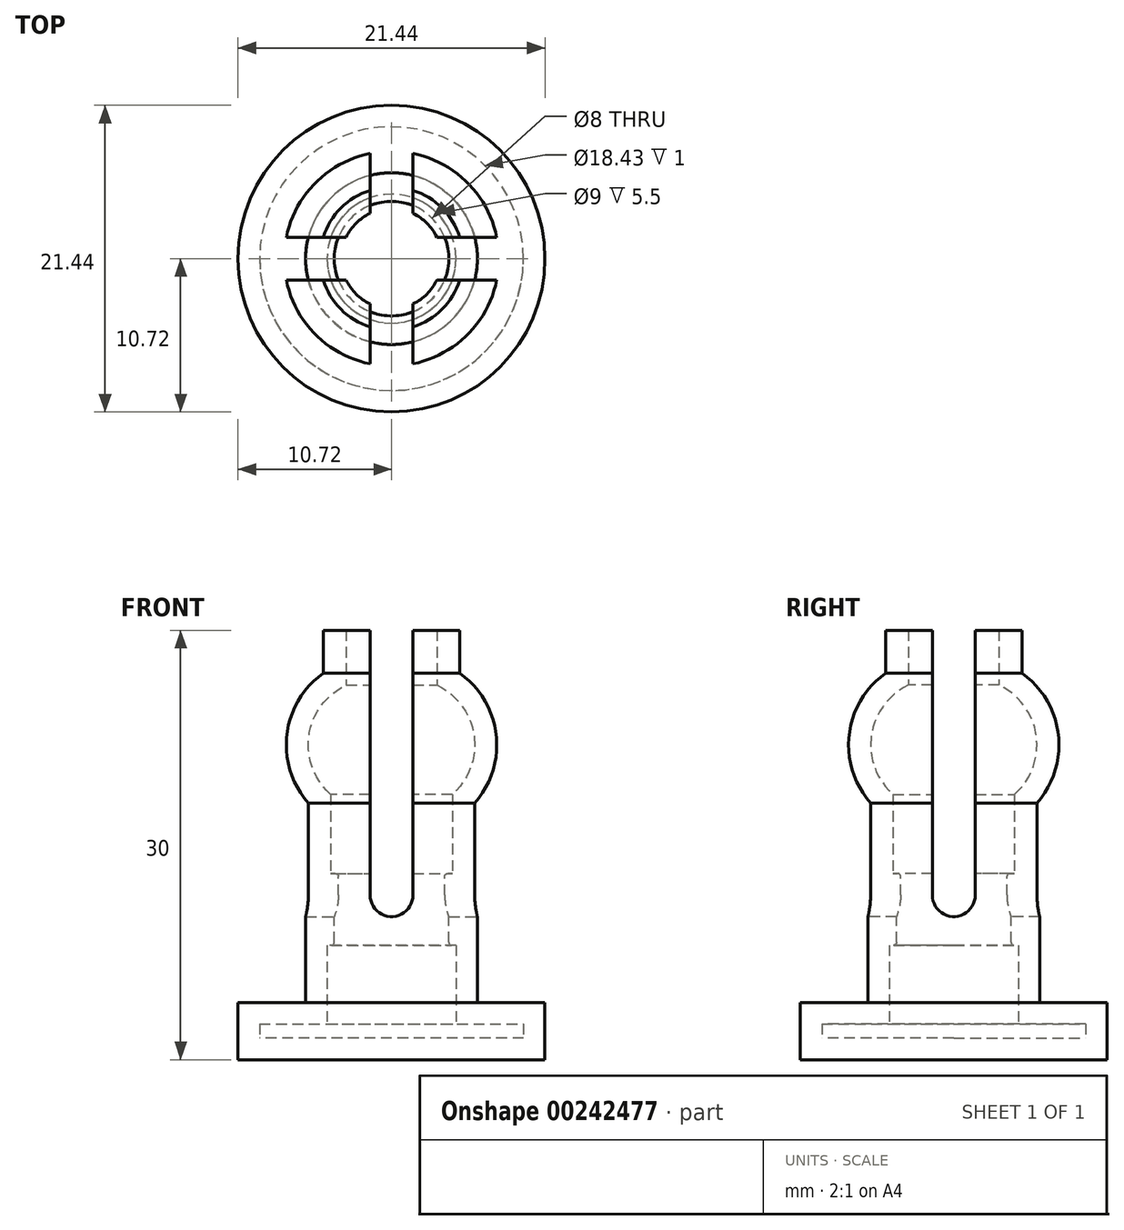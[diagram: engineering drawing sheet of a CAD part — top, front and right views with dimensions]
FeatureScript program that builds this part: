
annotation { "Feature Type Name" : "Feature", "Feature Type Description" : "" }
export const myFeature = defineFeature(function(context is Context, id is Id, definition is map)
    precondition{}
    {
        {
            var Q0;
            Q0=qCreatedBy(makeId("Front.planeOp"),FACE);
            var sketch = newSketch(context, id + "F0", { "sketchPlane" : qUnion([Q0])});
            skLineSegment(sketch, "E0", {"start": v(0, 8.33) * mm, "end": v(5, 8.33) * mm});
            skLineSegment(sketch, "E1", {"start": v(5, 8.33) * mm, "end": v(5, 5.33) * mm});
            skArc(sketch, "E2", {"start": v(6, -3.73) * mm, "mid": v(7.46, 1.02) * mm, "end": v(5, 5.33) * mm});
            skLineSegment(sketch, "E3", {"start": v(6, -17.67) * mm, "end": v(10.72, -17.67) * mm});
            skLineSegment(sketch, "E4", {"start": v(10.72, -17.67) * mm, "end": v(10.72, -21.67) * mm});
            skLineSegment(sketch, "E5", {"start": v(10.72, -21.67) * mm, "end": v(0, -21.67) * mm});
            skLineSegment(sketch, "E6", {"start": v(0, -21.67) * mm, "end": v(0, 8.33) * mm});
            skLineSegment(sketch, "E7", {"start": v(0, 22.23) * mm, "end": v(0, -23.28) * mm, "construction": true});
            skLineSegment(sketch, "E8", {"start": v(6, -17.67) * mm, "end": v(6, -3.73) * mm});
            skPoint(sketch, "E9.start.orphan", {"position": v(5, -4.67) * mm});
            skSolve(sketch);
        }
        {
            var Q0;
            Q0=qCreatedBy(makeId("Front.planeOp"),FACE);
            var sketch = newSketch(context, id + "F1", { "sketchPlane" : qUnion([Q0])});
            skLineSegment(sketch, "E10", {"start": v(0, 8.33) * mm, "end": v(5, 8.33) * mm});
            skLineSegment(sketch, "E11", {"start": v(5, 8.33) * mm, "end": v(5, 5.33) * mm});
            skArc(sketch, "E12", {"start": v(6, -3.73) * mm, "mid": v(7.46, 1.02) * mm, "end": v(5, 5.33) * mm});
            skLineSegment(sketch, "E13", {"start": v(6, -17.67) * mm, "end": v(10.72, -17.67) * mm});
            skLineSegment(sketch, "E14", {"start": v(10.72, -17.67) * mm, "end": v(10.72, -21.67) * mm});
            skLineSegment(sketch, "E15", {"start": v(10.72, -21.67) * mm, "end": v(0, -21.67) * mm});
            skLineSegment(sketch, "E16", {"start": v(0, -21.67) * mm, "end": v(0, 8.33) * mm});
            skLineSegment(sketch, "E17", {"start": v(0, 21.89) * mm, "end": v(0, -23.62) * mm, "construction": true});
            skLineSegment(sketch, "E18", {"start": v(6, -3.73) * mm, "end": v(6, -17.67) * mm});
            skSolve(sketch);
        }
        {
            var Q0;
            Q0=qCreatedBy(makeId("Front.planeOp"),FACE);
            var sketch = newSketch(context, id + "F2", { "sketchPlane" : qUnion([Q0])});
            skArc(sketch, "E19.0", {"start": v(7, -2.8) * mm, "mid": v(7.67, 1.65) * mm, "end": v(5.3, 5.48) * mm});
            skLineSegment(sketch, "E20.0", {"start": v(5.3, 8.63) * mm, "end": v(5.3, 5.48) * mm});
            skLineSegment(sketch, "E21.0", {"start": v(0, 8.63) * mm, "end": v(5.3, 8.63) * mm});
            skArc(sketch, "E22", {"start": v(0, 12.9) * mm, "mid": v(11.42, 4.57) * mm, "end": v(7, -8.85) * mm});
            skLineSegment(sketch, "E23", {"start": v(0, 12.9) * mm, "end": v(0, 8.63) * mm});
            skLineSegment(sketch, "E24", {"start": v(7, -8.85) * mm, "end": v(7, -2.8) * mm});
            skSolve(sketch);
        }
        {
            var Q0;
            Q0=makeQuery(id+"F0.imprint","IMPRINT",FACE,{"disambiguationData":[TD([[makeQuery(id+"F0.imprint","IMPRINT",EDGE,{"derivedFrom":sQuery(id+"F0.wireOp",EDGE,"E0")}),-1.0]])]});
            var Q1;
            Q1=sQuery(id+"F1.wireOp",EDGE,"E16");
            revolve(context, id + "F3", {"entities" : qUnion([Q0]), "axis" : qUnion([Q1]), "revolveType" : RevolveType.FULL});
        }
        {
            var Q0;
            Q0=makeQuery(id+"F2.imprint","IMPRINT",FACE,{"disambiguationData":[TD([[makeQuery(id+"F2.imprint","IMPRINT",EDGE,{"derivedFrom":sQuery(id+"F2.wireOp",EDGE,"E19.0")}),-1.0]])]});
            var Q1;
            Q1=sQuery(id+"F2.wireOp",EDGE,"E23");
            revolve(context, id + "F4", {"entities" : qUnion([Q0]), "axis" : qUnion([Q1]), "revolveType" : RevolveType.FULL});
        }
        {
            var Q0;
            Q0=qCreatedBy(makeId("Front.planeOp"),FACE);
            var sketch = newSketch(context, id + "F5", { "sketchPlane" : qUnion([Q0])});
            skLineSegment(sketch, "E25.bottom", {"start": v(-1.5, 8.33) * mm, "end": v(1.5, 8.33) * mm});
            skLineSegment(sketch, "E25.left", {"start": v(-1.5, 8.33) * mm, "end": v(-1.5, -10.17) * mm});
            skLineSegment(sketch, "E25.right", {"start": v(1.5, 8.33) * mm, "end": v(1.5, -10.17) * mm});
            skLineSegment(sketch, "E26", {"start": v(0, 10.52) * mm, "end": v(0, -1.34) * mm, "construction": true});
            skArc(sketch, "E27", {"start": v(-1.5, -10.17) * mm, "mid": v(0, -11.67) * mm, "end": v(1.5, -10.17) * mm});
            skSolve(sketch);
        }
        {
            var Q0;
            Q0=makeQuery(id+"F3.opRevolve","SWEPT_FACE",FACE,{"disambiguationData":[OSD([sQuery(id+"F0.wireOp",EDGE,"E0")])]});
            shell(context, id + "F6", {"entities" : qUnion([Q0]), "thickness" : 1.5 * mm});
        }
        {
            var Q0;
            Q0=qCreatedBy(makeId("Front.planeOp"),FACE);
            var sketch = newSketch(context, id + "F7", { "sketchPlane" : qUnion([Q0])});
            skLineSegment(sketch, "E28.bottom", {"start": v(4.5, -8.67) * mm, "end": v(4, -8.67) * mm});
            skLineSegment(sketch, "E28.top", {"start": v(4.5, -13.67) * mm, "end": v(4, -13.67) * mm});
            skLineSegment(sketch, "E28.left", {"start": v(4.5, -8.67) * mm, "end": v(4.5, -13.67) * mm});
            skLineSegment(sketch, "E28.right", {"start": v(4, -8.67) * mm, "end": v(4, -13.67) * mm});
            skLineSegment(sketch, "E29", {"start": v(4.5, -19.17) * mm, "end": v(4.5, -3.13) * mm, "construction": true});
            skSolve(sketch);
        }
        {
            var Q0;
            Q0 = qSketchRegion(id + "F7", true);
            var Q1;
            Q1=makeQuery(id+"F6.opShell","OFFSET_EDGE",EDGE,{"disambiguationData":[OSD([sQuery(id+"F0.wireOp",EDGE,"E0"),sQuery(id+"F0.wireOp",EDGE,"E1")])]});
            revolve(context, id + "F8", {"operationType" : NewBodyOperationType.ADD, "entities" : qUnion([Q0]), "axis" : qUnion([Q1]), "revolveType" : RevolveType.FULL});
        }
        {
            var Q0;
            Q0=makeQuery(id+"F8.opRevolve","SWEPT_EDGE",EDGE,{"disambiguationData":[OSD([sQuery(id+"F7.wireOp",EDGE,"E28.bottom"),sQuery(id+"F7.wireOp",EDGE,"E28.right")])]});
            var Q1;
            Q1=makeQuery(id+"F8.opRevolve","SWEPT_EDGE",EDGE,{"disambiguationData":[OSD([sQuery(id+"F7.wireOp",EDGE,"E28.top"),sQuery(id+"F7.wireOp",EDGE,"E28.right")])]});
            fillet(context, id + "F9", {"entities" : qUnion([Q0, Q1]), "radius" : .2 * mm, "tangentPropagation" : true, "allowEdgeOverflow" : false});
        }
        {
            var Q0;
            Q0 = qSketchRegion(id + "F5", true);
            extrude(context, id + "F10", {"entities" : qUnion([Q0]), "operationType" : NewBodyOperationType.REMOVE, "endBound" : BoundingType.SYMMETRIC, "oppositeDirection" : true, "depth" : 25 * mm});
        }
        {
            var Q0;
            Q0=qCreatedBy(makeId("Right.planeOp"),FACE);
            var sketch = newSketch(context, id + "F11", { "sketchPlane" : qUnion([Q0])});
            skLineSegment(sketch, "E30.bottom", {"start": v(-1.5, 8.33) * mm, "end": v(1.5, 8.33) * mm});
            skLineSegment(sketch, "E30.left", {"start": v(-1.5, 8.33) * mm, "end": v(-1.5, -10.17) * mm});
            skLineSegment(sketch, "E30.right", {"start": v(1.5, 8.33) * mm, "end": v(1.5, -10.17) * mm});
            skLineSegment(sketch, "E31", {"start": v(0, 10.52) * mm, "end": v(0, -1.34) * mm, "construction": true});
            skArc(sketch, "E32", {"start": v(-1.5, -10.17) * mm, "mid": v(0, -11.67) * mm, "end": v(1.5, -10.17) * mm});
            skSolve(sketch);
        }
        {
            var Q0;
            Q0 = qSketchRegion(id + "F11", true);
            extrude(context, id + "F12", {"entities" : qUnion([Q0]), "operationType" : NewBodyOperationType.REMOVE, "endBound" : BoundingType.SYMMETRIC, "oppositeDirection" : true, "depth" : 25 * mm});
        }
        {
            var Q0;
            Q0=makeQuery(id+"F4.opRevolve","SWEPT_BODY",BODY,{"disambiguationData":[OSD([sQuery(id+"F2.wireOp",EDGE,"E19.0"),sQuery(id+"F2.wireOp",EDGE,"E20.0"),sQuery(id+"F2.wireOp",EDGE,"E21.0"),sQuery(id+"F2.wireOp",EDGE,"E22"),sQuery(id+"F2.wireOp",EDGE,"E23"),sQuery(id+"F2.wireOp",EDGE,"E24")])]});
            deleteBodies(context, id + "F13", {"entities" : qUnion([Q0])});
        }
    });
